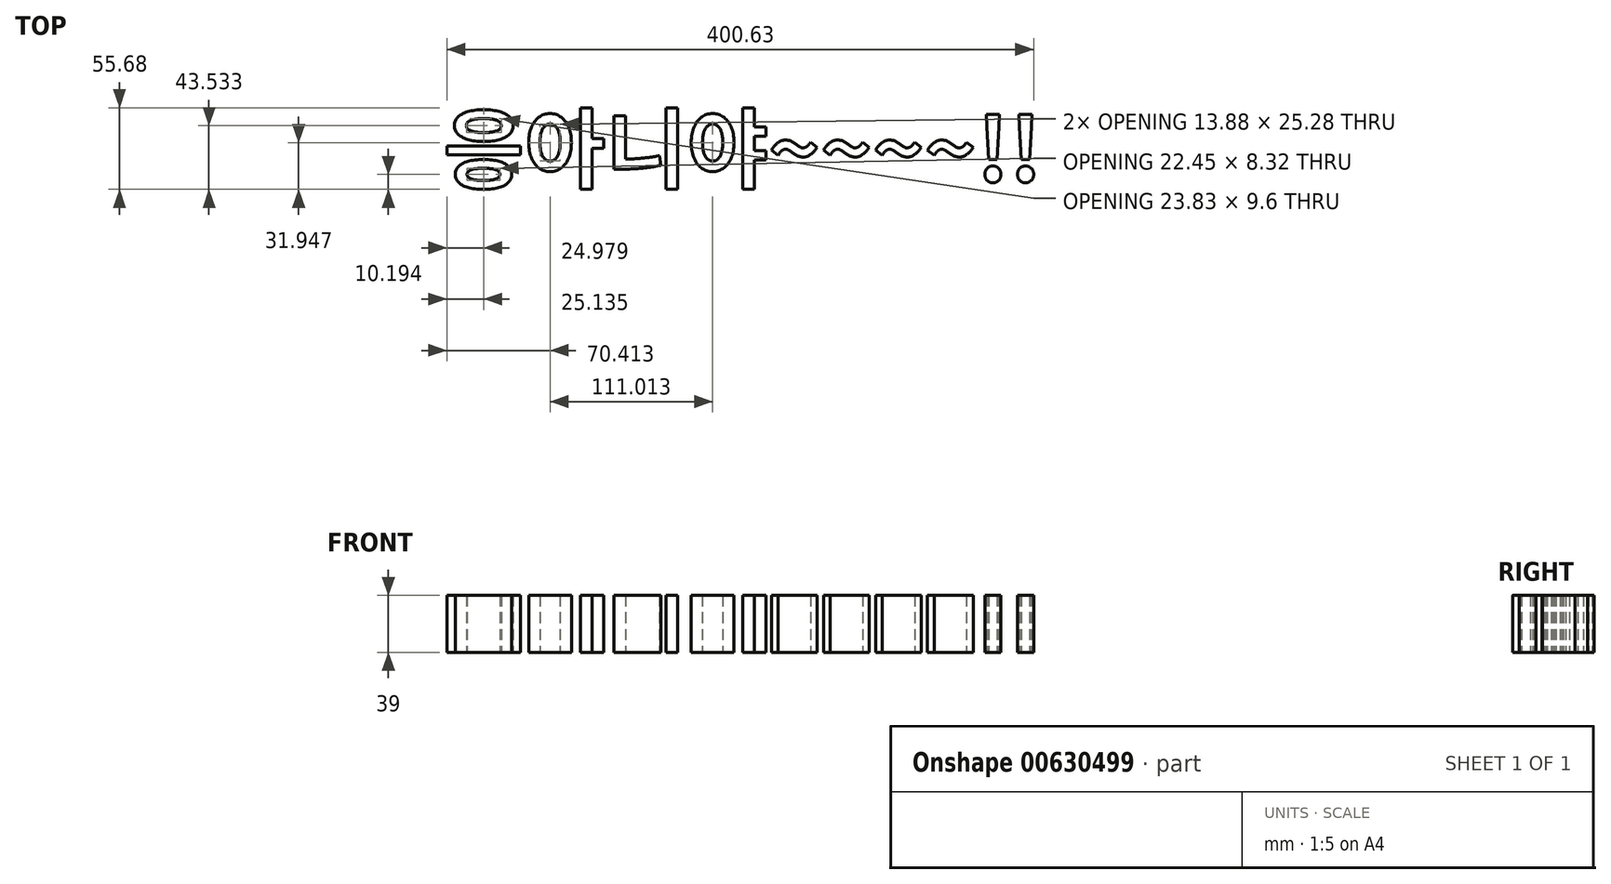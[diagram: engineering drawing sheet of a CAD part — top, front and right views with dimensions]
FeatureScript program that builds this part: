
annotation { "Feature Type Name" : "Feature", "Feature Type Description" : "" }
export const myFeature = defineFeature(function(context is Context, id is Id, definition is map)
    precondition{}
    {
        {
            var Q0;
            Q0=qCreatedBy(makeId("Top.planeOp"),FACE);
            var sketch = newSketch(context, id + "F0", { "sketchPlane" : qUnion([Q0])});
            skText(sketch, "E0", { "text": "응아니야~~~~!!", "fontName": "NotoSansCJKkr-Bold.otf"});
            const initialGuessF0  = {"E0": [-0.07511, -0.02029, 1, 0, 0.04344]};
            skSetInitialGuess(sketch, initialGuessF0);
            skSolve(sketch);
        }
        {
            var Q0;
            Q0 = qSketchRegion(id + "F0", true);
            extrude(context, id + "F1", {"entities" : qUnion([Q0]), "depth" : 39 * mm, "offsetDistance" : 25 * mm});
        }
    });
